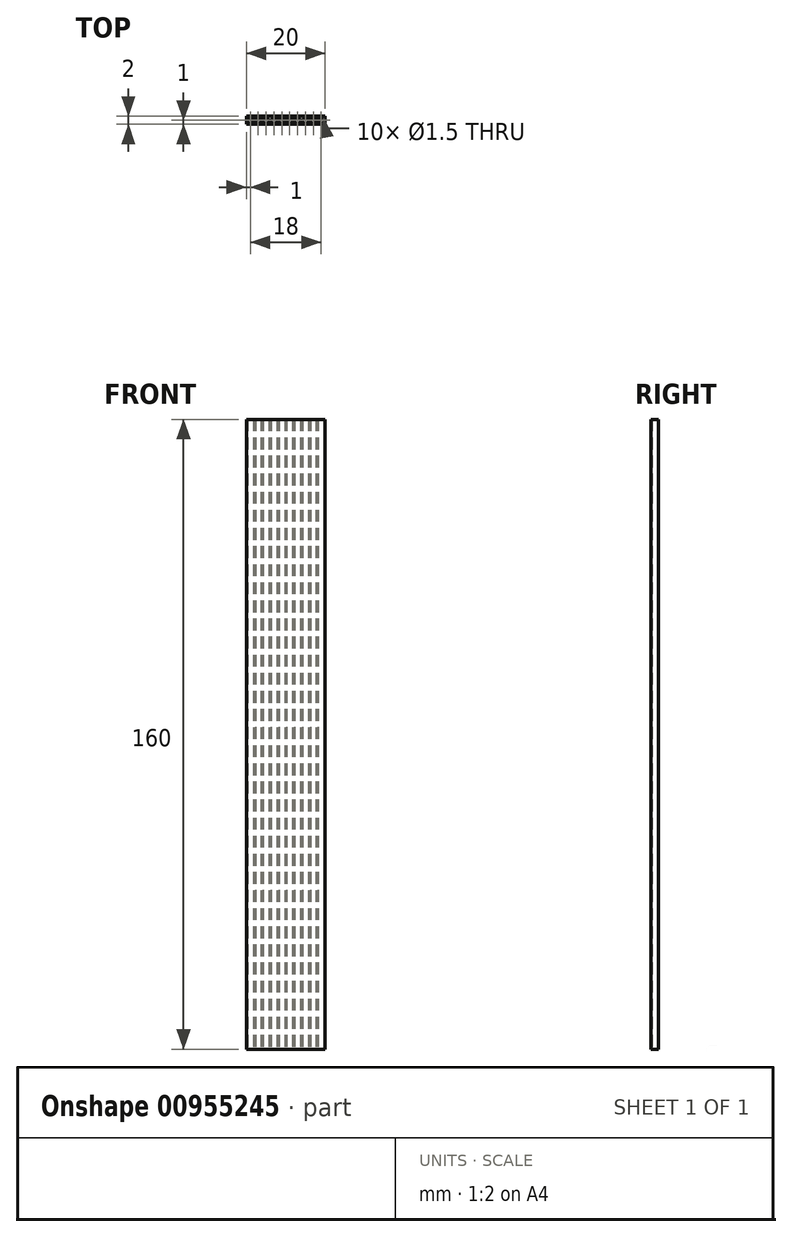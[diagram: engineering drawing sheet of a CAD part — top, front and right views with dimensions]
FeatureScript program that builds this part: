
annotation { "Feature Type Name" : "Feature", "Feature Type Description" : "" }
export const myFeature = defineFeature(function(context is Context, id is Id, definition is map)
    precondition{}
    {
        {
            var Q0;
            Q0=qCreatedBy(makeId("Top.planeOp"),FACE);
            var sketch = newSketch(context, id + "F0", { "sketchPlane" : qUnion([Q0])});
            skLineSegment(sketch, "E0.bottom", {"start": v(0, 0) * mm, "end": v(-20, 0) * mm});
            skLineSegment(sketch, "E0.top", {"start": v(0, 2) * mm, "end": v(-20, 2) * mm});
            skLineSegment(sketch, "E0.left", {"start": v(0, 0) * mm, "end": v(0, 2) * mm});
            skLineSegment(sketch, "E0.right", {"start": v(-20, 0) * mm, "end": v(-20, 2) * mm});
            skCircle(sketch, "E1", {"center": v(-19, 1) * mm, "radius": 0.75 * mm});
            skCircle(sketch, "E2.1.0.0", {"center": v(-17, 1) * mm, "radius": 0.75 * mm});
            skCircle(sketch, "E2.2.0.0", {"center": v(-15, 1) * mm, "radius": 0.75 * mm});
            skCircle(sketch, "E2.3.0.0", {"center": v(-13, 1) * mm, "radius": 0.75 * mm});
            skCircle(sketch, "E2.4.0.0", {"center": v(-11, 1) * mm, "radius": 0.75 * mm});
            skCircle(sketch, "E2.5.0.0", {"center": v(-9, 1) * mm, "radius": 0.75 * mm});
            skCircle(sketch, "E2.6.0.0", {"center": v(-7, 1) * mm, "radius": 0.75 * mm});
            skCircle(sketch, "E2.7.0.0", {"center": v(-5, 1) * mm, "radius": 0.75 * mm});
            skCircle(sketch, "E2.8.0.0", {"center": v(-3, 1) * mm, "radius": 0.75 * mm});
            skCircle(sketch, "E2.9.0.0", {"center": v(-1, 1) * mm, "radius": 0.75 * mm});
            skLineSegment(sketch, "E2.direction1", {"start": v(-19, 1) * mm, "end": v(-17, 1) * mm, "construction": true});
            skSolve(sketch);
        }
        {
            var Q0;
            Q0=makeQuery(id+"F0.imprint","IMPRINT",FACE,{"disambiguationData":[TD([[makeQuery(id+"F0.imprint","IMPRINT",EDGE,{"derivedFrom":sQuery(id+"F0.wireOp",EDGE,"E0.bottom")}),-1.0]])]});
            extrude(context, id + "F1", {"entities" : qUnion([Q0]), "depth" : 160 * mm, "offsetDistance" : 25 * mm});
        }
    });
